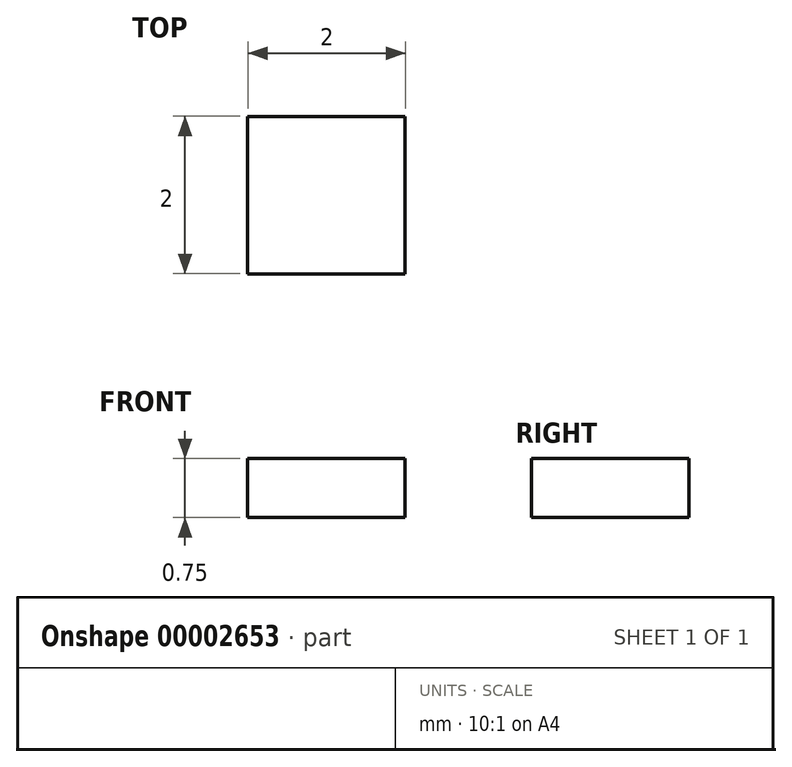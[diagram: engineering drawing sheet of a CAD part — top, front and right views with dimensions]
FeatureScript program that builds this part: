
annotation { "Feature Type Name" : "Feature", "Feature Type Description" : "" }
export const myFeature = defineFeature(function(context is Context, id is Id, definition is map)
    precondition{}
    {
        {
            var Q0;
            Q0=qCreatedBy(makeId("Top.planeOp"),FACE);
            var sketch = newSketch(context, id + "F0", { "sketchPlane" : qUnion([Q0])});
            skLineSegment(sketch, "E0.bottom", {"start": v(-1.1, 1.42) * mm, "end": v(0.9, 1.42) * mm});
            skLineSegment(sketch, "E0.top", {"start": v(-1.1, -0.58) * mm, "end": v(0.9, -0.58) * mm});
            skLineSegment(sketch, "E0.left", {"start": v(-1.1, 1.42) * mm, "end": v(-1.1, -0.58) * mm});
            skLineSegment(sketch, "E0.right", {"start": v(0.9, 1.42) * mm, "end": v(0.9, -0.58) * mm});
            skSolve(sketch);
        }
        {
            var Q0;
            Q0=makeQuery(id+"F0.imprint","IMPRINT",FACE,{"disambiguationData":[TD([[makeQuery(id+"F0.imprint","IMPRINT",EDGE,{"derivedFrom":sQuery(id+"F0.wireOp",EDGE,"E0.bottom")}),-1.0]])]});
            extrude(context, id + "F1", {"entities" : qUnion([Q0]), "depth" : .75 * mm});
        }
    });
